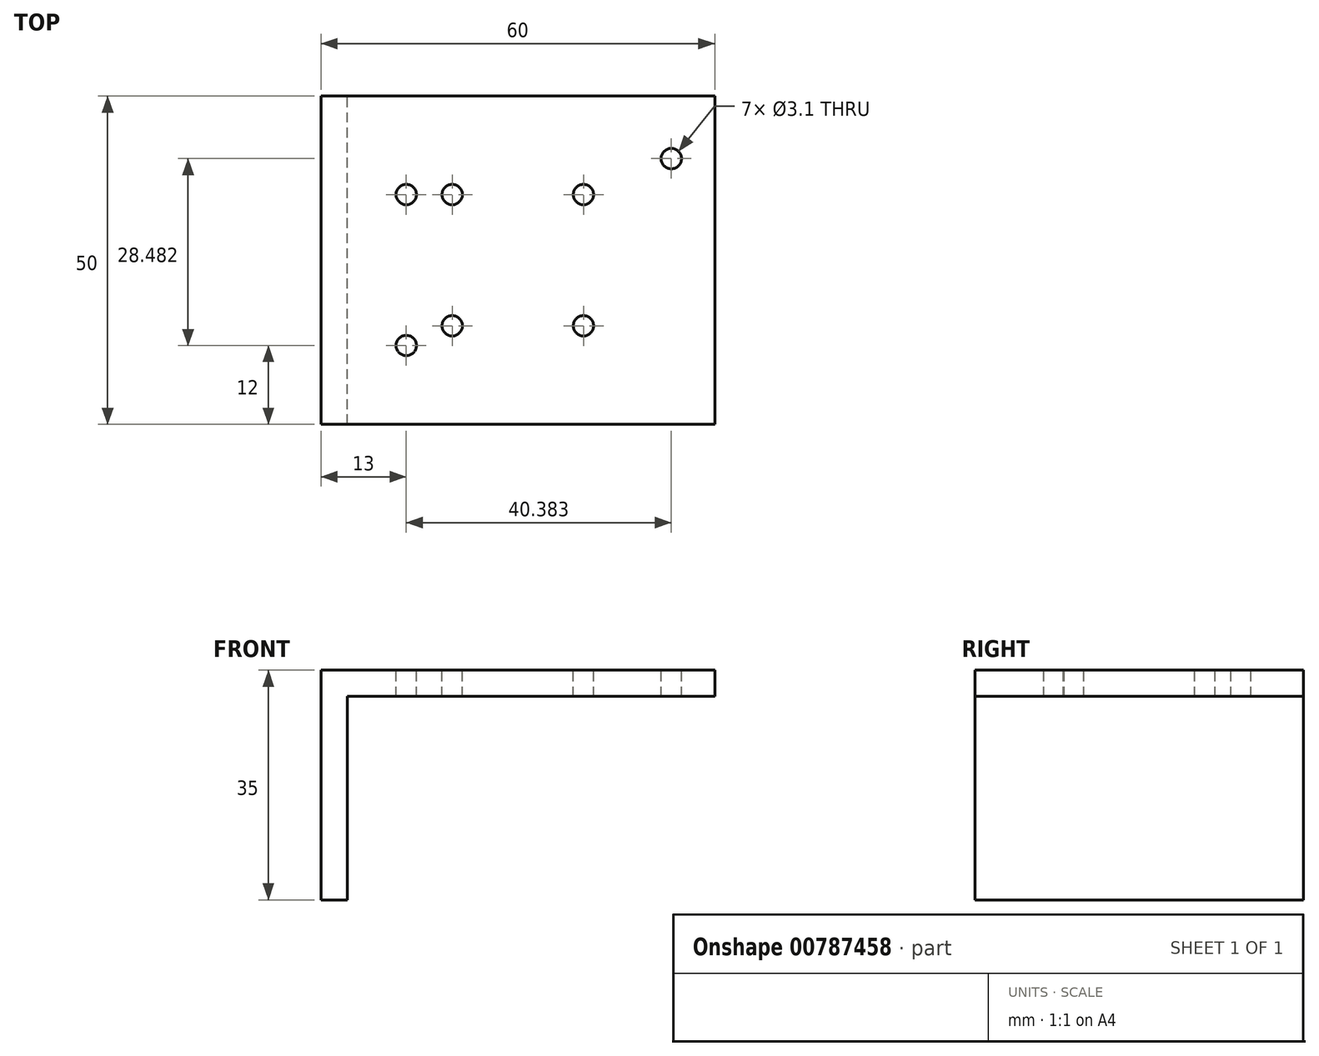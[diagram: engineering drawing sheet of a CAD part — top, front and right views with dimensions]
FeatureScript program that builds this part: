
annotation { "Feature Type Name" : "Feature", "Feature Type Description" : "" }
export const myFeature = defineFeature(function(context is Context, id is Id, definition is map)
    precondition{}
    {
        {
            var Q0;
            Q0=qCreatedBy(makeId("Front.planeOp"),FACE);
            var sketch = newSketch(context, id + "F0", { "sketchPlane" : qUnion([Q0])});
            skLineSegment(sketch, "E0", {"start": v(0, 0) * mm, "end": v(0, -35) * mm});
            skLineSegment(sketch, "E1", {"start": v(0, -35) * mm, "end": v(4, -35) * mm});
            skLineSegment(sketch, "E2", {"start": v(4, -35) * mm, "end": v(4, -4) * mm});
            skLineSegment(sketch, "E3", {"start": v(4, -4) * mm, "end": v(60, -4) * mm});
            skLineSegment(sketch, "E4", {"start": v(60, -4) * mm, "end": v(60, 0) * mm});
            skLineSegment(sketch, "E5", {"start": v(60, 0) * mm, "end": v(0, 0) * mm});
            skSolve(sketch);
        }
        {
            var Q0;
            Q0=makeQuery(id+"F0.imprint","IMPRINT",FACE,{"disambiguationData":[TD([[makeQuery(id+"F0.imprint","IMPRINT",EDGE,{"derivedFrom":sQuery(id+"F0.wireOp",EDGE,"E0")}),1.0]])]});
            extrude(context, id + "F1", {"entities" : qUnion([Q0]), "depth" : 50 * mm, "offsetDistance" : 25 * mm});
        }
        {
            var Q0;
            Q0=makeQuery(id+"F1.opExtrude","SWEPT_FACE",FACE,{"disambiguationData":[OSD([sQuery(id+"F0.wireOp",EDGE,"E5")])]});
            var sketch = newSketch(context, id + "F2", { "sketchPlane" : qUnion([Q0])});
            skLineSegment(sketch, "E6", {"start": v(0, -25) * mm, "end": v(60, -25) * mm, "construction": true});
            skLineSegment(sketch, "E7", {"start": v(30, 0) * mm, "end": v(30, -50) * mm, "construction": true});
            skCircle(sketch, "E8", {"center": v(40, -15) * mm, "radius": 1.55 * mm});
            skCircle(sketch, "E9.MirrorC", {"center": v(20, -15) * mm, "radius": 1.55 * mm});
            skCircle(sketch, "E10.MirrorC", {"center": v(20, -35) * mm, "radius": 1.55 * mm});
            skCircle(sketch, "E11.MirrorC", {"center": v(40, -35) * mm, "radius": 1.55 * mm});
            skLineSegment(sketch, "E12", {"start": v(13, -50) * mm, "end": v(13, 0) * mm, "construction": true});
            skCircle(sketch, "E13", {"center": v(13, -38) * mm, "radius": 1.55 * mm});
            skCircle(sketch, "E14", {"center": v(13, -15) * mm, "radius": 1.55 * mm});
            skCircle(sketch, "E15", {"center": v(53.38, -9.52) * mm, "radius": 1.55 * mm});
            skSolve(sketch);
        }
        {
            var Q0;
            Q0 = qSketchRegion(id + "F2", true);
            extrude(context, id + "F3", {"entities" : qUnion([Q0]), "operationType" : NewBodyOperationType.REMOVE, "endBound" : BoundingType.UP_TO_NEXT, "oppositeDirection" : true, "depth" : 25 * mm, "offsetDistance" : 25 * mm});
        }
    });
